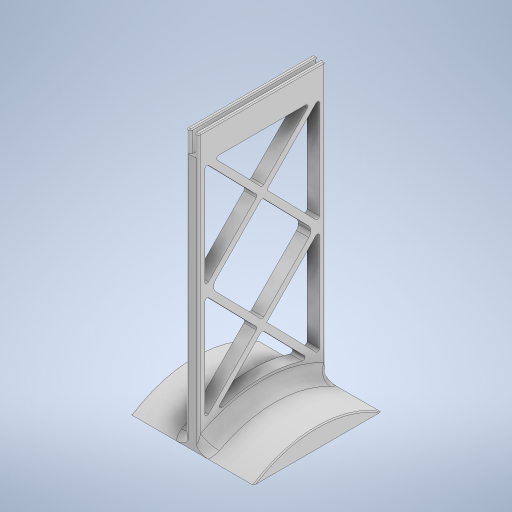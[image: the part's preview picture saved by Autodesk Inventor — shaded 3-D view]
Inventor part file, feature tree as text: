
AUTODESK INVENTOR PART (.ipt)
format: ipt  version: 2023 (Build 270158000, 158)  size: 546,816 bytes
history: native  units: mm
features: fillet x6, extrude x5, sketch x5, plane x1, mirror x1, chamfer x1
ambient origin geometry x8: Origin, YZ Plane, XZ Plane, XY Plane, X Axis, Y Axis, Z Axis, Center Point
bodies: Solid1 (feature_tree)
feature tree (19):
  extrude  "Extrusion1"  Depth=130.0mm
  sketch  "Sketch2"  dims[d2=5.8mm d3=0.0mm d4=60.0mm]
  extrude  "Extrusion2"  Depth=5.8mm
  plane  "Work Plane1"
  mirror  "Mirror1"
  extrude  "Extrusion4"  Depth=26.0mm TaperAngle=0.0deg
  extrude  "Extrusion5"  Depth=10.0mm TaperAngle=0.0deg
  extrude  "Extrusion6"  Depth=3.0mm
  fillet  "Fillet1"  Radius=3.0mm
  fillet  "Fillet2"  Radius=3.0mm
  fillet  "Fillet4"  [1 undecoded]
  chamfer  "Chamfer1"  Angle=45.0deg  [1 undecoded]
  fillet  "Fillet5"  Radius=4.0mm
  fillet  "Fillet6"  [1 undecoded]
  fillet  "Fillet7"  Radius=1.0mm
  sketch  "Sketch1"  dims[d0=60.0mm d1=130.0mm]
  sketch  "Sketch4"  dims[d5=55.0mm d6=26.0mm d7=0.0mm]
  sketch  "Sketch5"  dims[d10=1.8mm d11=10.0mm d12=0.0mm]
  sketch  "Sketch6"  dims[d13=1.0mm d18=3.0mm d19=3.0mm d21=3.0mm d22=45.0deg d23=45.0deg d24=3.0mm d25=3.0mm d26=3.0mm d27=45.0deg d28=45.0deg d29=3.0mm d30=3.0mm d31=3.0mm d32=45.0deg d33=45.0deg d34=4.0mm d35=4.0mm d38=3.0mm d39=3.0mm d40=3.0mm d41=45.0deg d42=45.0deg d43=4.0mm d44=0.0mm d45=0.0mm d47=1.0mm d49=-2.9mm d50=6.0mm d51=0.5mm d52=2.0mm d53=45.0deg d54=0.5mm d55=3.0mm d56=3.0mm d57=16.0mm d58=3.0mm d59=3.0mm d60=3.0mm d61=3.0mm d63=3.0mm d64=3.0mm d65=3.0mm d66=3.0mm d67=26.0mm d68=0.0mm d69=12.0mm d70=65.0mm d71=1.0mm d72=3.0mm]
note: 3 required parameter values undecoded (feature->parameter linkage not recoverable at this tier; creation-order binding heuristic only, values carry confidence <= 0.55)
